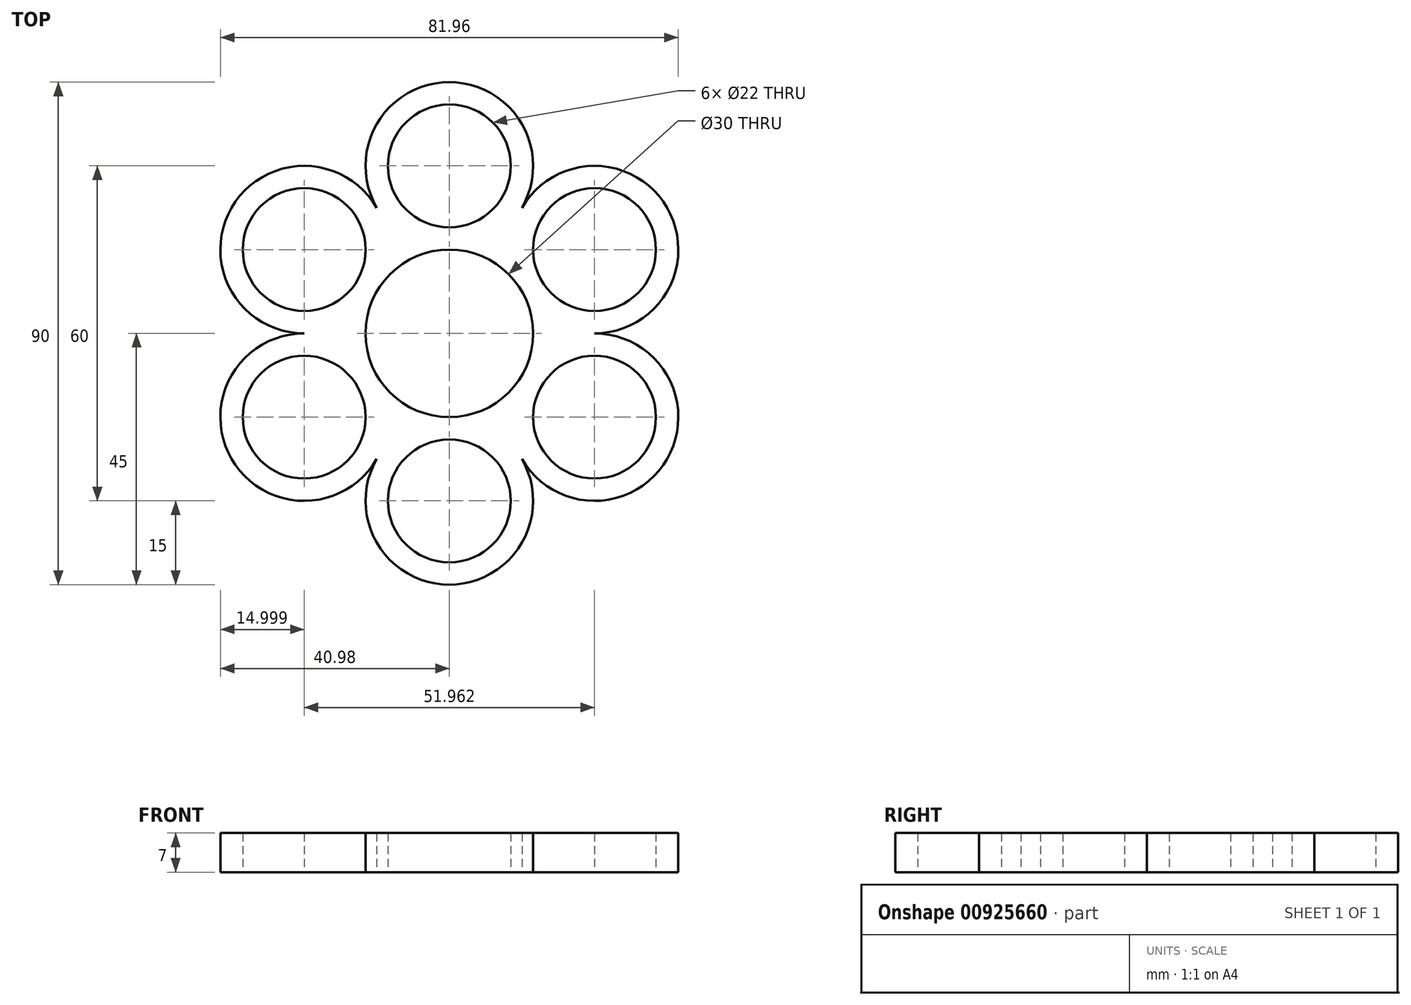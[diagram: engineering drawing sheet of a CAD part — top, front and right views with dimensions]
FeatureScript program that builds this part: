
annotation { "Feature Type Name" : "Feature", "Feature Type Description" : "" }
export const myFeature = defineFeature(function(context is Context, id is Id, definition is map)
    precondition{}
    {
        {
            var Q0;
            Q0=qCreatedBy(makeId("Top.planeOp"),FACE);
            var sketch = newSketch(context, id + "F0", { "sketchPlane" : qUnion([Q0])});
            skArc(sketch, "E0", {"start": v(5.5, 9.53) * mm, "mid": v(0, 11) * mm, "end": v(-5.5, 9.53) * mm});
            skCircle(sketch, "E1", {"center": v(0, 30) * mm, "radius": 11 * mm});
            skArc(sketch, "E2", {"start": v(13, 22.5) * mm, "mid": v(0, 45) * mm, "end": v(-13, 22.5) * mm});
            skArc(sketch, "E3", {"start": v(7.5, 13) * mm, "mid": v(0, 15) * mm, "end": v(-7.5, 13) * mm});
            skCircle(sketch, "E4.1.0", {"center": v(-25.98, 15) * mm, "radius": 11 * mm});
            skArc(sketch, "E4.1.1", {"start": v(-13, 22.5) * mm, "mid": v(-38.97, 22.5) * mm, "end": v(-25.98, 0) * mm});
            skArc(sketch, "E4.1.2", {"start": v(-7.5, 13) * mm, "mid": v(-13, 7.5) * mm, "end": v(-15, 0) * mm});
            skArc(sketch, "E4.1.3", {"start": v(-5.5, 9.53) * mm, "mid": v(-9.53, 5.5) * mm, "end": v(-11, 0) * mm});
            skCircle(sketch, "E4.2.0", {"center": v(-25.98, -15) * mm, "radius": 11 * mm});
            skArc(sketch, "E4.2.1", {"start": v(-25.98, 0) * mm, "mid": v(-38.97, -22.5) * mm, "end": v(-13, -22.5) * mm});
            skArc(sketch, "E4.2.2", {"start": v(-15, 0) * mm, "mid": v(-13, -7.5) * mm, "end": v(-7.5, -13) * mm});
            skArc(sketch, "E4.2.3", {"start": v(-11, 0) * mm, "mid": v(-9.53, -5.5) * mm, "end": v(-5.5, -9.53) * mm});
            skCircle(sketch, "E4.3.0", {"center": v(0, -30) * mm, "radius": 11 * mm});
            skArc(sketch, "E4.3.1", {"start": v(-13, -22.5) * mm, "mid": v(0, -45) * mm, "end": v(13, -22.5) * mm});
            skArc(sketch, "E4.3.2", {"start": v(-7.5, -13) * mm, "mid": v(0, -15) * mm, "end": v(7.5, -13) * mm});
            skArc(sketch, "E4.3.3", {"start": v(-5.5, -9.53) * mm, "mid": v(0, -11) * mm, "end": v(5.5, -9.53) * mm});
            skCircle(sketch, "E4.4.0", {"center": v(25.98, -15) * mm, "radius": 11 * mm});
            skArc(sketch, "E4.4.1", {"start": v(13, -22.5) * mm, "mid": v(38.97, -22.5) * mm, "end": v(25.98, 0) * mm});
            skArc(sketch, "E4.4.2", {"start": v(7.5, -13) * mm, "mid": v(13, -7.5) * mm, "end": v(15, 0) * mm});
            skArc(sketch, "E4.4.3", {"start": v(5.5, -9.53) * mm, "mid": v(9.53, -5.5) * mm, "end": v(11, 0) * mm});
            skCircle(sketch, "E4.5.0", {"center": v(25.98, 15) * mm, "radius": 11 * mm});
            skArc(sketch, "E4.5.1", {"start": v(25.98, 0) * mm, "mid": v(38.97, 22.5) * mm, "end": v(13, 22.5) * mm});
            skArc(sketch, "E4.5.2", {"start": v(15, 0) * mm, "mid": v(13, 7.5) * mm, "end": v(7.5, 13) * mm});
            skArc(sketch, "E4.5.3", {"start": v(11, 0) * mm, "mid": v(9.53, 5.5) * mm, "end": v(5.5, 9.53) * mm});
            skSolve(sketch);
        }
        {
            var Q0;
            Q0 = qSketchRegion(id + "F0", true);
            extrude(context, id + "F1", {"entities" : qUnion([Q0]), "depth" : 7 * mm, "offsetDistance" : 25 * mm});
        }
    });
